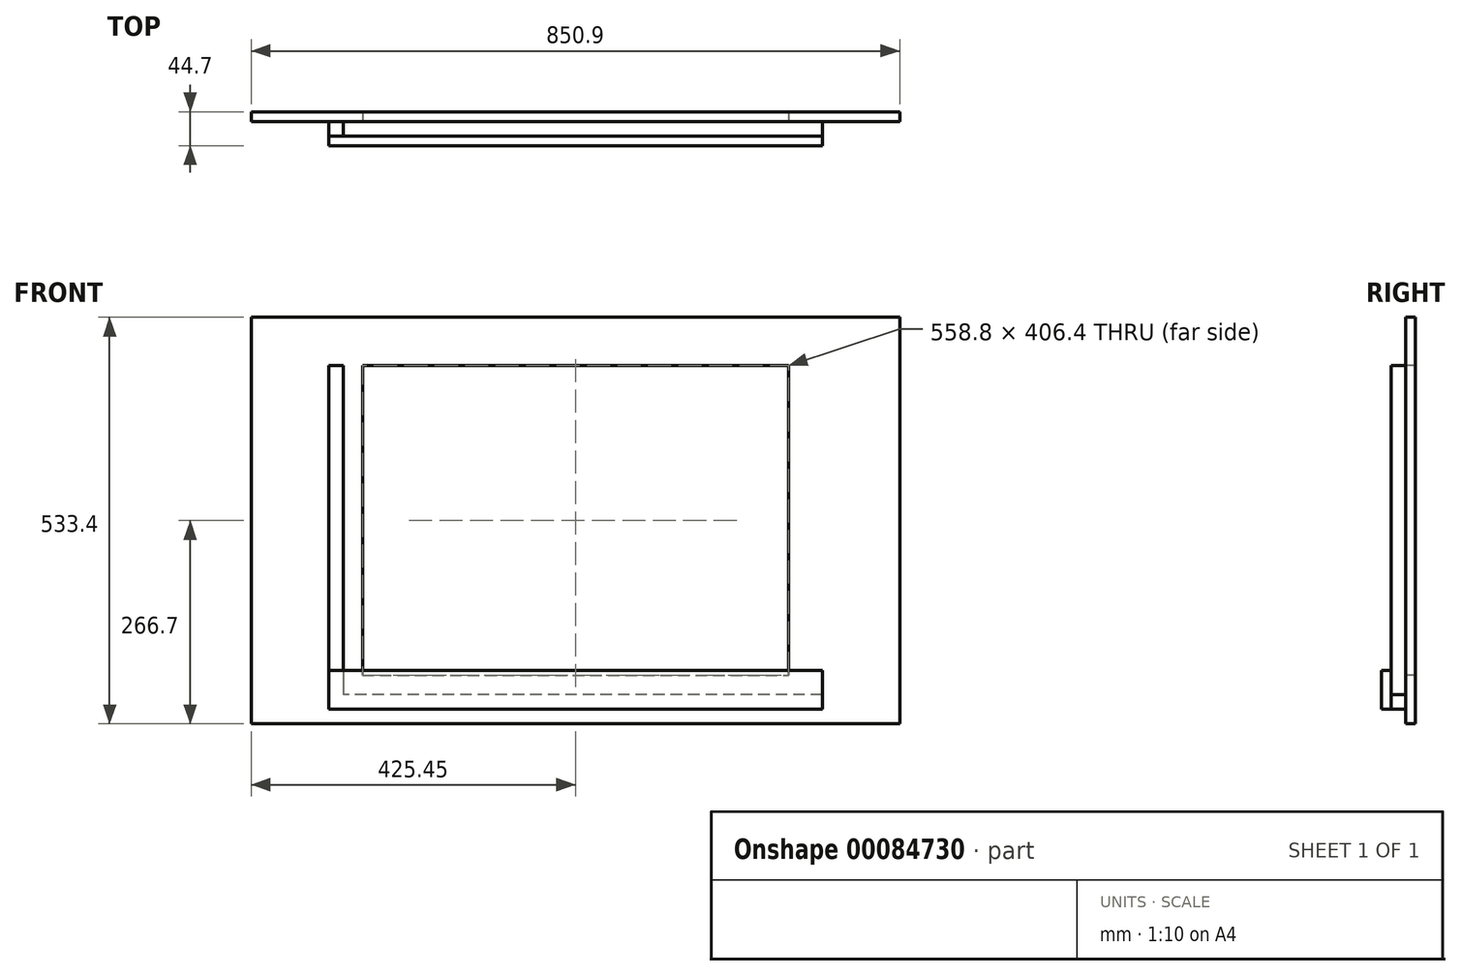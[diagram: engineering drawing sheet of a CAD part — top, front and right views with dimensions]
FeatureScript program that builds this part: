
annotation { "Feature Type Name" : "Feature", "Feature Type Description" : "" }
export const myFeature = defineFeature(function(context is Context, id is Id, definition is map)
    precondition{}
    {
        {
            var Q0;
            Q0=qCreatedBy(makeId("Front.planeOp"),FACE);
            var sketch = newSketch(context, id + "F0", { "sketchPlane" : qUnion([Q0])});
            skLineSegment(sketch, "E0.bottom", {"start": v(-425.45, 266.7) * mm, "end": v(425.45, 266.7) * mm});
            skLineSegment(sketch, "E0.top", {"start": v(-425.45, -266.7) * mm, "end": v(425.45, -266.7) * mm});
            skLineSegment(sketch, "E0.left", {"start": v(-425.45, 266.7) * mm, "end": v(-425.45, -266.7) * mm});
            skLineSegment(sketch, "E0.right", {"start": v(425.45, 266.7) * mm, "end": v(425.45, -266.7) * mm});
            skSolve(sketch);
        }
        {
            var Q0;
            Q0=makeQuery(id+"F0.imprint","IMPRINT",FACE,{"disambiguationData":[TD([[makeQuery(id+"F0.imprint","IMPRINT",EDGE,{"derivedFrom":sQuery(id+"F0.wireOp",EDGE,"E0.bottom")}),-1.0]])]});
            extrude(context, id + "F1", {"entities" : qUnion([Q0]), "depth" : 12.7 * mm});
        }
        {
            var Q0;
            Q0=makeQuery(id+"F1.opExtrude","CAP_FACE",FACE,{"disambiguationData":[OSD([sQuery(id+"F0.wireOp",EDGE,"E0.bottom"),sQuery(id+"F0.wireOp",EDGE,"E0.top"),sQuery(id+"F0.wireOp",EDGE,"E0.left"),sQuery(id+"F0.wireOp",EDGE,"E0.right")])],"isStart":false});
            var sketch = newSketch(context, id + "F2", { "sketchPlane" : qUnion([Q0])});
            skLineSegment(sketch, "E1.bottom", {"start": v(-279.4, 203.2) * mm, "end": v(279.4, 203.2) * mm});
            skLineSegment(sketch, "E1.top", {"start": v(-279.4, -203.2) * mm, "end": v(279.4, -203.2) * mm});
            skLineSegment(sketch, "E1.left", {"start": v(-279.4, 203.2) * mm, "end": v(-279.4, -203.2) * mm});
            skLineSegment(sketch, "E1.right", {"start": v(279.4, 203.2) * mm, "end": v(279.4, -203.2) * mm});
            skSolve(sketch);
        }
        {
            var Q0;
            Q0=makeQuery(id+"F2.imprint","IMPRINT",FACE,{"disambiguationData":[TD([[makeQuery(id+"F2.imprint","IMPRINT",EDGE,{"derivedFrom":sQuery(id+"F2.wireOp",EDGE,"E1.bottom")}),-1.0]])]});
            extrude(context, id + "F3", {"entities" : qUnion([Q0]), "operationType" : NewBodyOperationType.REMOVE, "endBound" : BoundingType.UP_TO_NEXT, "oppositeDirection" : true, "depth" : 25.4 * mm});
        }
        {
            var Q0;
            Q0=makeQuery(id+"F1.opExtrude","CAP_FACE",FACE,{"disambiguationData":[OSD([sQuery(id+"F0.wireOp",EDGE,"E0.bottom"),sQuery(id+"F0.wireOp",EDGE,"E0.top"),sQuery(id+"F0.wireOp",EDGE,"E0.left"),sQuery(id+"F0.wireOp",EDGE,"E0.right")])],"isStart":false});
            var sketch = newSketch(context, id + "F4", { "sketchPlane" : qUnion([Q0])});
            skLineSegment(sketch, "E2.bottom", {"start": v(-323.85, 203.2) * mm, "end": v(-304.8, 203.2) * mm});
            skLineSegment(sketch, "E2.top", {"start": v(-323.85, -228.6) * mm, "end": v(-304.8, -228.6) * mm});
            skLineSegment(sketch, "E2.left", {"start": v(-323.85, 203.2) * mm, "end": v(-323.85, -228.6) * mm});
            skLineSegment(sketch, "E2.right", {"start": v(-304.8, 203.2) * mm, "end": v(-304.8, -228.6) * mm});
            skLineSegment(sketch, "E3.bottom", {"start": v(323.85, -228.6) * mm, "end": v(-323.85, -228.6) * mm});
            skLineSegment(sketch, "E3.top", {"start": v(323.85, -247.65) * mm, "end": v(-323.85, -247.65) * mm});
            skLineSegment(sketch, "E3.left", {"start": v(323.85, -228.6) * mm, "end": v(323.85, -247.65) * mm});
            skLineSegment(sketch, "E3.right", {"start": v(-323.85, -228.6) * mm, "end": v(-323.85, -247.65) * mm});
            skLineSegment(sketch, "E4.bottom", {"start": v(323.85, -228.6) * mm, "end": v(304.8, -228.6) * mm});
            skLineSegment(sketch, "E4.top", {"start": v(323.85, 203.2) * mm, "end": v(304.8, 203.2) * mm});
            skLineSegment(sketch, "E4.left", {"start": v(323.85, -228.6) * mm, "end": v(323.85, 203.2) * mm});
            skLineSegment(sketch, "E4.right", {"start": v(304.8, -228.6) * mm, "end": v(304.8, 203.2) * mm});
            skSolve(sketch);
        }
        {
            var Q0;
            Q0=makeQuery(id+"F4.imprint","IMPRINT",FACE,{"disambiguationData":[TD([[makeQuery(id+"F4.imprint","IMPRINT",EDGE,{"derivedFrom":sQuery(id+"F4.wireOp",EDGE,"E2.bottom")}),-1.0]])]});
            var Q1;
            Q1=makeQuery(id+"F4.imprint","IMPRINT",FACE,{"disambiguationData":[TD([[makeQuery(id+"F4.imprint","IMPRINT",EDGE,{"derivedFrom":sQuery(id+"F4.wireOp",EDGE,"E3.top")}),-1.0]])]});
            var Q2;
            Q2=makeQuery(id+"F4.imprint","IMPRINT",FACE,{"disambiguationData":[TD([[makeQuery(id+"F4.imprint","IMPRINT",EDGE,{"derivedFrom":sQuery(id+"F4.wireOp",EDGE,"E4.bottom")}),-1.0]])]});
            extrude(context, id + "F5", {"entities" : qUnion([Q0, Q1, Q2]), "depth" : 19.3 * mm});
        }
        {
            var Q0;
            Q0=makeQuery(id+"F5.opExtrude","CAP_FACE",FACE,{"disambiguationData":[OSD([sQuery(id+"F4.wireOp",EDGE,"E2.bottom"),sQuery(id+"F4.wireOp",EDGE,"E2.left"),sQuery(id+"F4.wireOp",EDGE,"E2.right"),sQuery(id+"F4.wireOp",EDGE,"E3.bottom"),sQuery(id+"F4.wireOp",EDGE,"E3.top"),sQuery(id+"F4.wireOp",EDGE,"E3.left"),sQuery(id+"F4.wireOp",EDGE,"E3.right"),sQuery(id+"F4.wireOp",EDGE,"E4.top"),sQuery(id+"F4.wireOp",EDGE,"E4.left"),sQuery(id+"F4.wireOp",EDGE,"E4.right")])],"isStart":false});
            var sketch = newSketch(context, id + "F6", { "sketchPlane" : qUnion([Q0])});
            skLineSegment(sketch, "E5.bottom", {"start": v(-323.85, -247.65) * mm, "end": v(323.85, -247.65) * mm});
            skLineSegment(sketch, "E5.top", {"start": v(-323.85, -196.85) * mm, "end": v(323.85, -196.85) * mm});
            skLineSegment(sketch, "E5.left", {"start": v(-323.85, -247.65) * mm, "end": v(-323.85, -196.85) * mm});
            skLineSegment(sketch, "E5.right", {"start": v(323.85, -247.65) * mm, "end": v(323.85, -196.85) * mm});
            skSolve(sketch);
        }
        {
            var Q0;
            {var subQ5=makeQuery(id+"F5.opExtrude","CAP_EDGE",EDGE,{"disambiguationData":[OSD([sQuery(id+"F4.wireOp",EDGE,"E3.bottom")])],"isStart":false});Q0=makeQuery(id+"F6.imprint","IMPRINT",FACE,{"disambiguationData":[TD([[makeQuery(id+"F6.imprint","IMPRINT",EDGE,{"derivedFrom":subQ5}),-1.0]])]});}
            var Q1;
            Q1=makeQuery(id+"F6.imprint","IMPRINT",FACE,{"disambiguationData":[TD([[makeQuery(id+"F6.imprint","IMPRINT",EDGE,{"derivedFrom":sQuery(id+"F6.wireOp",EDGE,"E5.bottom")}),-1.0]])]});
            extrude(context, id + "F7", {"entities" : qUnion([Q0, Q1]), "depth" : 12.7 * mm});
        }
    });
